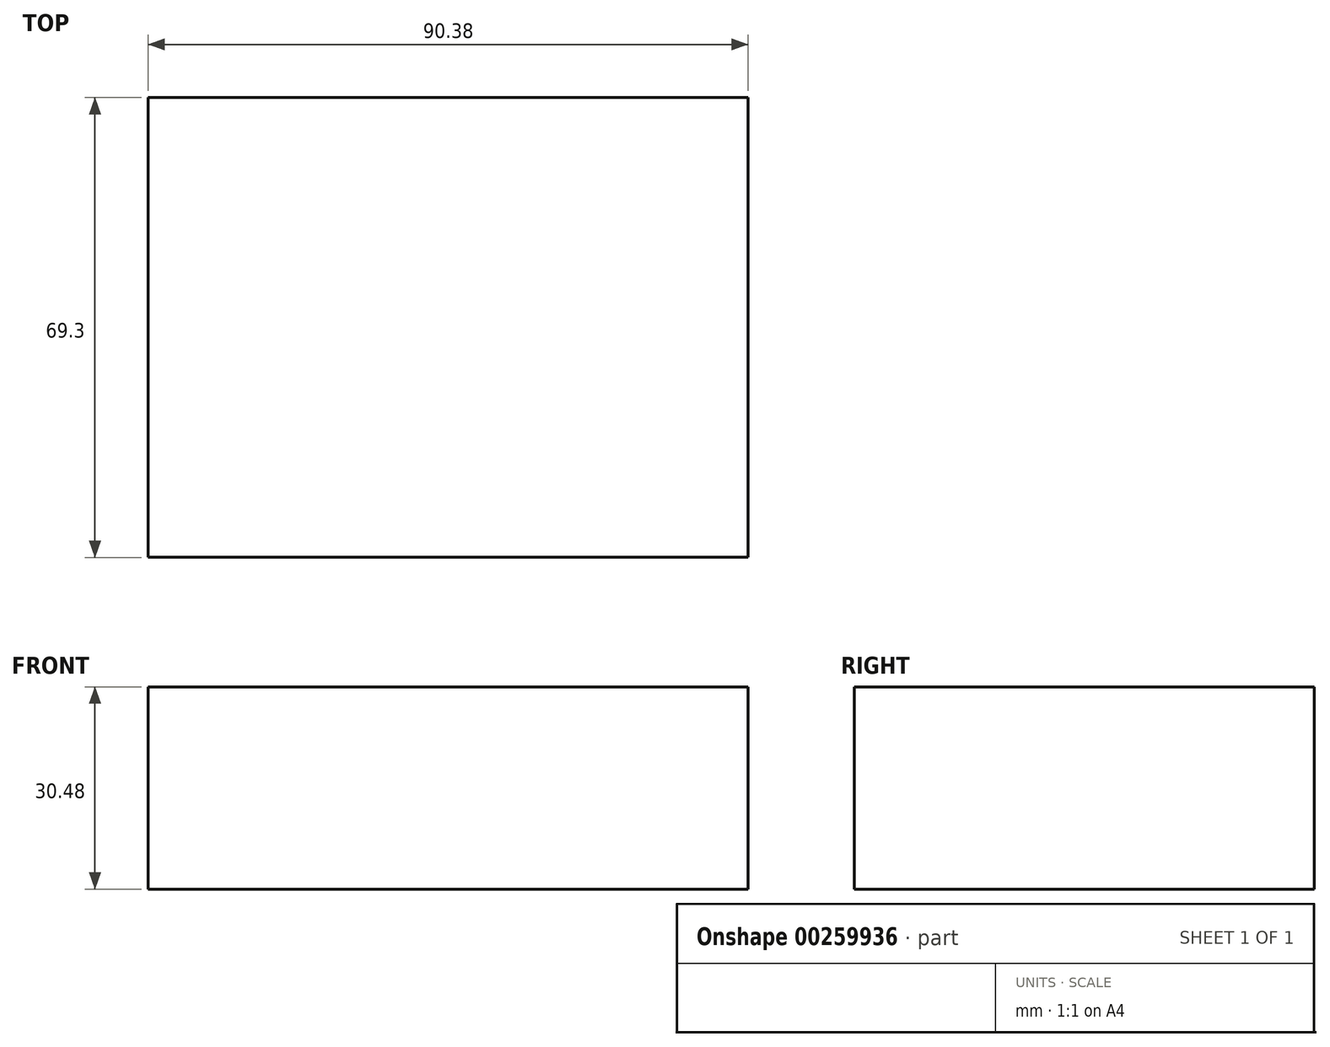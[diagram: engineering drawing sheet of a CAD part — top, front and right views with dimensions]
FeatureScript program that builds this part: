
annotation { "Feature Type Name" : "Feature", "Feature Type Description" : "" }
export const myFeature = defineFeature(function(context is Context, id is Id, definition is map)
    precondition{}
    {
        {
            var Q0;
            Q0=qCreatedBy(makeId("Top.planeOp"),FACE);
            var sketch = newSketch(context, id + "F0", { "sketchPlane" : qUnion([Q0])});
            skLineSegment(sketch, "E0.bottom", {"start": v(45.19, 34.65) * mm, "end": v(-45.19, 34.65) * mm});
            skLineSegment(sketch, "E0.top", {"start": v(45.19, -34.65) * mm, "end": v(-45.19, -34.65) * mm});
            skLineSegment(sketch, "E0.left", {"start": v(45.19, 34.65) * mm, "end": v(45.19, -34.65) * mm});
            skLineSegment(sketch, "E0.right", {"start": v(-45.19, 34.65) * mm, "end": v(-45.19, -34.65) * mm});
            skPoint(sketch, "E0.middle", {"position": v(0, 0) * mm});
            skSolve(sketch);
        }
        {
            var Q0;
            Q0 = qSketchRegion(id + "F0", true);
            extrude(context, id + "F1", {"entities" : qUnion([Q0]), "depth" : 30.48 * mm});
        }
    });
